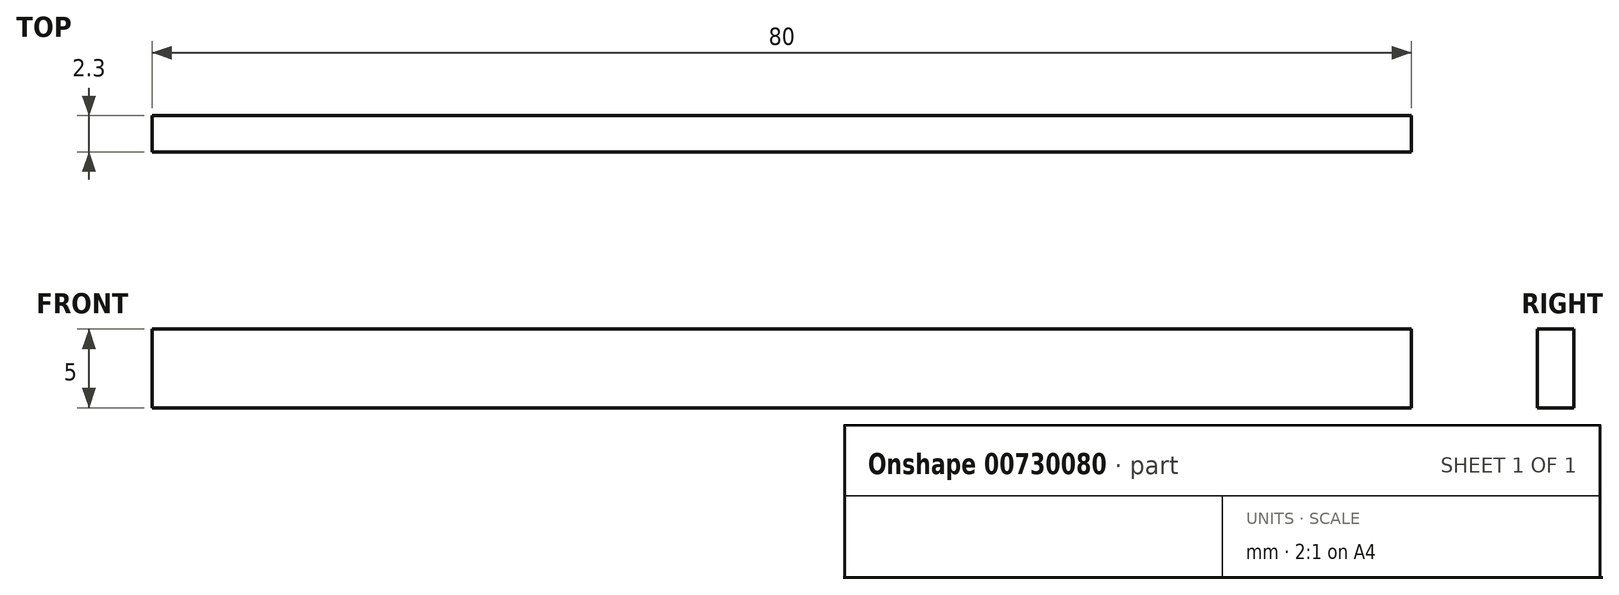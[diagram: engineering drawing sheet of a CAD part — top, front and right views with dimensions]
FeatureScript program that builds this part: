
annotation { "Feature Type Name" : "Feature", "Feature Type Description" : "" }
export const myFeature = defineFeature(function(context is Context, id is Id, definition is map)
    precondition{}
    {
        {
            var Q0;
            Q0=qCreatedBy(makeId("Top.planeOp"),FACE);
            var sketch = newSketch(context, id + "F0", { "sketchPlane" : qUnion([Q0])});
            skLineSegment(sketch, "E0.bottom", {"start": v(0, 0) * mm, "end": v(80, 0) * mm});
            skLineSegment(sketch, "E0.top", {"start": v(0, -2.3) * mm, "end": v(80, -2.3) * mm});
            skLineSegment(sketch, "E0.left", {"start": v(0, 0) * mm, "end": v(0, -2.3) * mm});
            skLineSegment(sketch, "E0.right", {"start": v(80, 0) * mm, "end": v(80, -2.3) * mm});
            skSolve(sketch);
        }
        {
            var Q0;
            Q0=makeQuery(id+"F0.imprint","IMPRINT",FACE,{"disambiguationData":[TD([[makeQuery(id+"F0.imprint","IMPRINT",EDGE,{"derivedFrom":sQuery(id+"F0.wireOp",EDGE,"E0.bottom")}),-1.0]])]});
            extrude(context, id + "F1", {"entities" : qUnion([Q0]), "depth" : 5 * mm, "offsetDistance" : 25 * mm});
        }
    });
